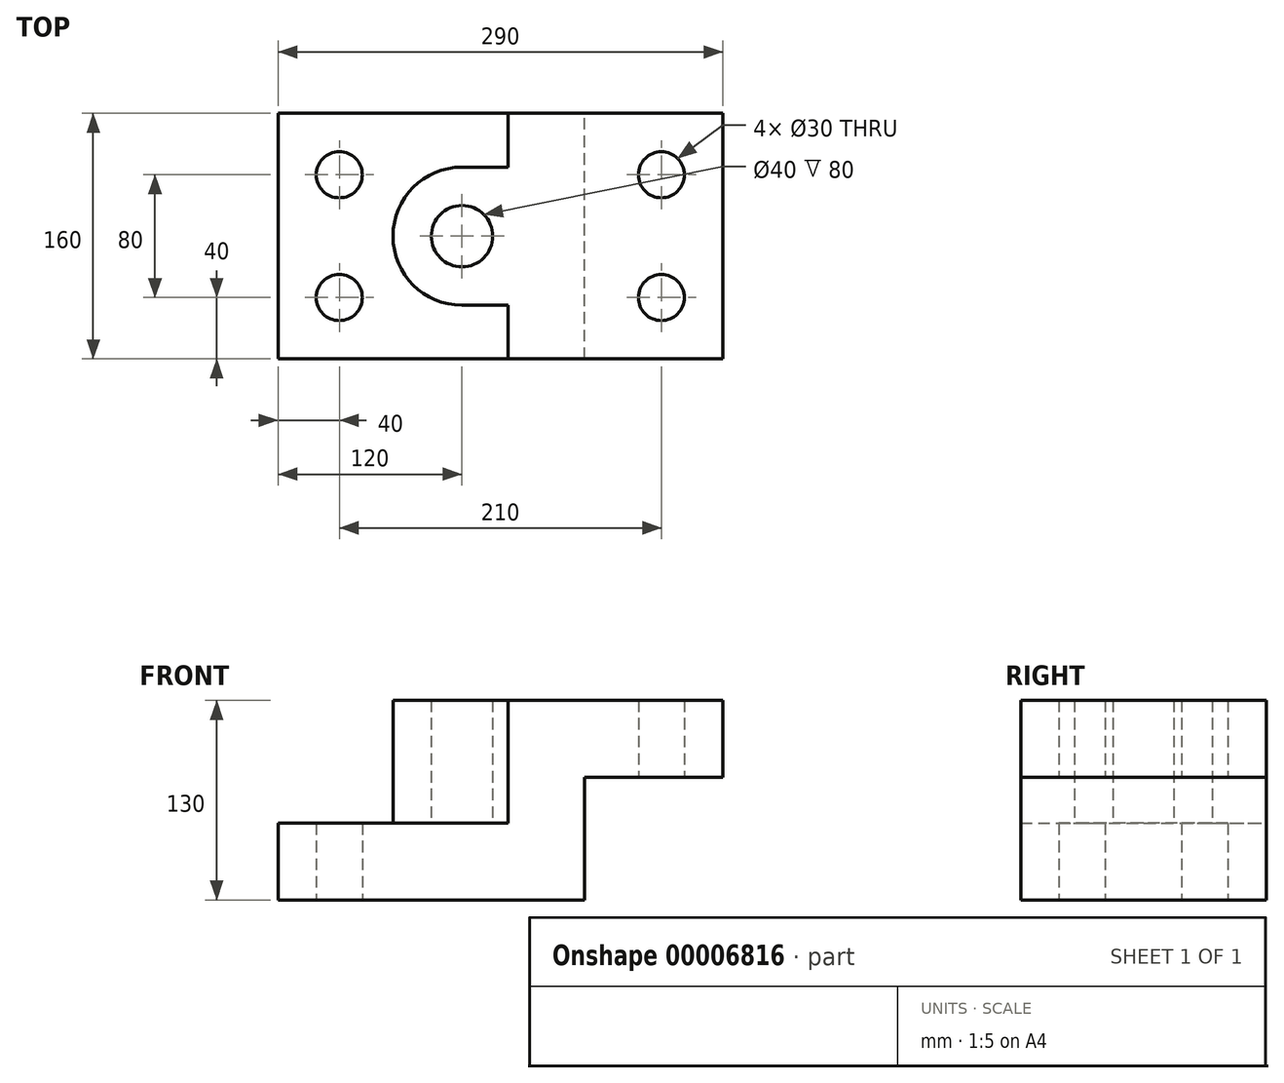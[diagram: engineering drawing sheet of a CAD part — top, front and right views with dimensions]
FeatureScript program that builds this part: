
annotation { "Feature Type Name" : "Feature", "Feature Type Description" : "" }
export const myFeature = defineFeature(function(context is Context, id is Id, definition is map)
    precondition{}
    {
        {
            var Q0;
            Q0=qCreatedBy(makeId("Front.planeOp"),FACE);
            var sketch = newSketch(context, id + "F0", { "sketchPlane" : qUnion([Q0])});
            skLineSegment(sketch, "E0", {"start": v(0, 0) * mm, "end": v(200, 0) * mm});
            skLineSegment(sketch, "E1", {"start": v(200, 0) * mm, "end": v(200, 80) * mm});
            skLineSegment(sketch, "E2", {"start": v(200, 80) * mm, "end": v(290, 80) * mm});
            skLineSegment(sketch, "E3", {"start": v(290, 80) * mm, "end": v(290, 130) * mm});
            skLineSegment(sketch, "E4", {"start": v(290, 130) * mm, "end": v(150, 130) * mm});
            skLineSegment(sketch, "E5", {"start": v(150, 130) * mm, "end": v(150, 50) * mm});
            skLineSegment(sketch, "E6", {"start": v(150, 50) * mm, "end": v(0, 50) * mm});
            skLineSegment(sketch, "E7", {"start": v(0, 50) * mm, "end": v(0, 0) * mm});
            skSolve(sketch);
        }
        {
            var Q0;
            Q0 = qSketchRegion(id + "F0", true);
            extrude(context, id + "F1", {"entities" : qUnion([Q0]), "depth" : 160 * mm, "symmetric" : true});
        }
        {
            var Q0;
            Q0=makeQuery(id+"F1.opExtrude","SWEPT_FACE",FACE,{"disambiguationData":[OSD([sQuery(id+"F0.wireOp",EDGE,"E6")])]});
            var sketch = newSketch(context, id + "F2", { "sketchPlane" : qUnion([Q0])});
            skLineSegment(sketch, "E8", {"start": v(150, 45) * mm, "end": v(150, -45) * mm});
            skLineSegment(sketch, "E9", {"start": v(150, -45) * mm, "end": v(120, -45) * mm});
            skArc(sketch, "E10", {"start": v(120, -45) * mm, "mid": v(75, 0) * mm, "end": v(120, 45) * mm});
            skLineSegment(sketch, "E11", {"start": v(120, 45) * mm, "end": v(150, 45) * mm});
            skCircle(sketch, "E12", {"center": v(120, 0) * mm, "radius": 20 * mm});
            skSolve(sketch);
        }
        {
            var Q0;
            Q0 = qSketchRegion(id + "F2", true);
            var Q1;
            Q1=makeQuery(id+"F1.opExtrude","SWEPT_FACE",FACE,{"disambiguationData":[OSD([sQuery(id+"F0.wireOp",EDGE,"E4")])]});
            extrude(context, id + "F3", {"entities" : qUnion([Q0]), "operationType" : NewBodyOperationType.ADD, "endBound" : BoundingType.UP_TO_SURFACE, "endBoundEntityFace" : qUnion([Q1]), "depth" : 25 * mm});
        }
        {
            var Q0;
            Q0=qCreatedBy(makeId("Top.planeOp"),FACE);
            var sketch = newSketch(context, id + "F4", { "sketchPlane" : qUnion([Q0])});
            skCircle(sketch, "E13", {"center": v(40, 40) * mm, "radius": 15 * mm});
            skCircle(sketch, "E14.0.1.0", {"center": v(40, -40) * mm, "radius": 15 * mm});
            skCircle(sketch, "E14.1.0.0", {"center": v(250, 40) * mm, "radius": 15 * mm});
            skCircle(sketch, "E14.1.1.0", {"center": v(250, -40) * mm, "radius": 15 * mm});
            skCircle(sketch, "E14.2.0.0", {"center": v(460, 40) * mm, "radius": 15 * mm});
            skCircle(sketch, "E14.2.1.0", {"center": v(460, -40) * mm, "radius": 15 * mm});
            skLineSegment(sketch, "E14.direction1", {"start": v(40, 40) * mm, "end": v(250, 40) * mm, "construction": true});
            skLineSegment(sketch, "E14.direction2", {"start": v(40, 40) * mm, "end": v(40, -40) * mm, "construction": true});
            skSolve(sketch);
        }
        {
            var Q0;
            Q0 = qSketchRegion(id + "F4", true);
            extrude(context, id + "F5", {"entities" : qUnion([Q0]), "operationType" : NewBodyOperationType.REMOVE, "endBound" : BoundingType.THROUGH_ALL, "depth" : 25 * mm});
        }
    });
